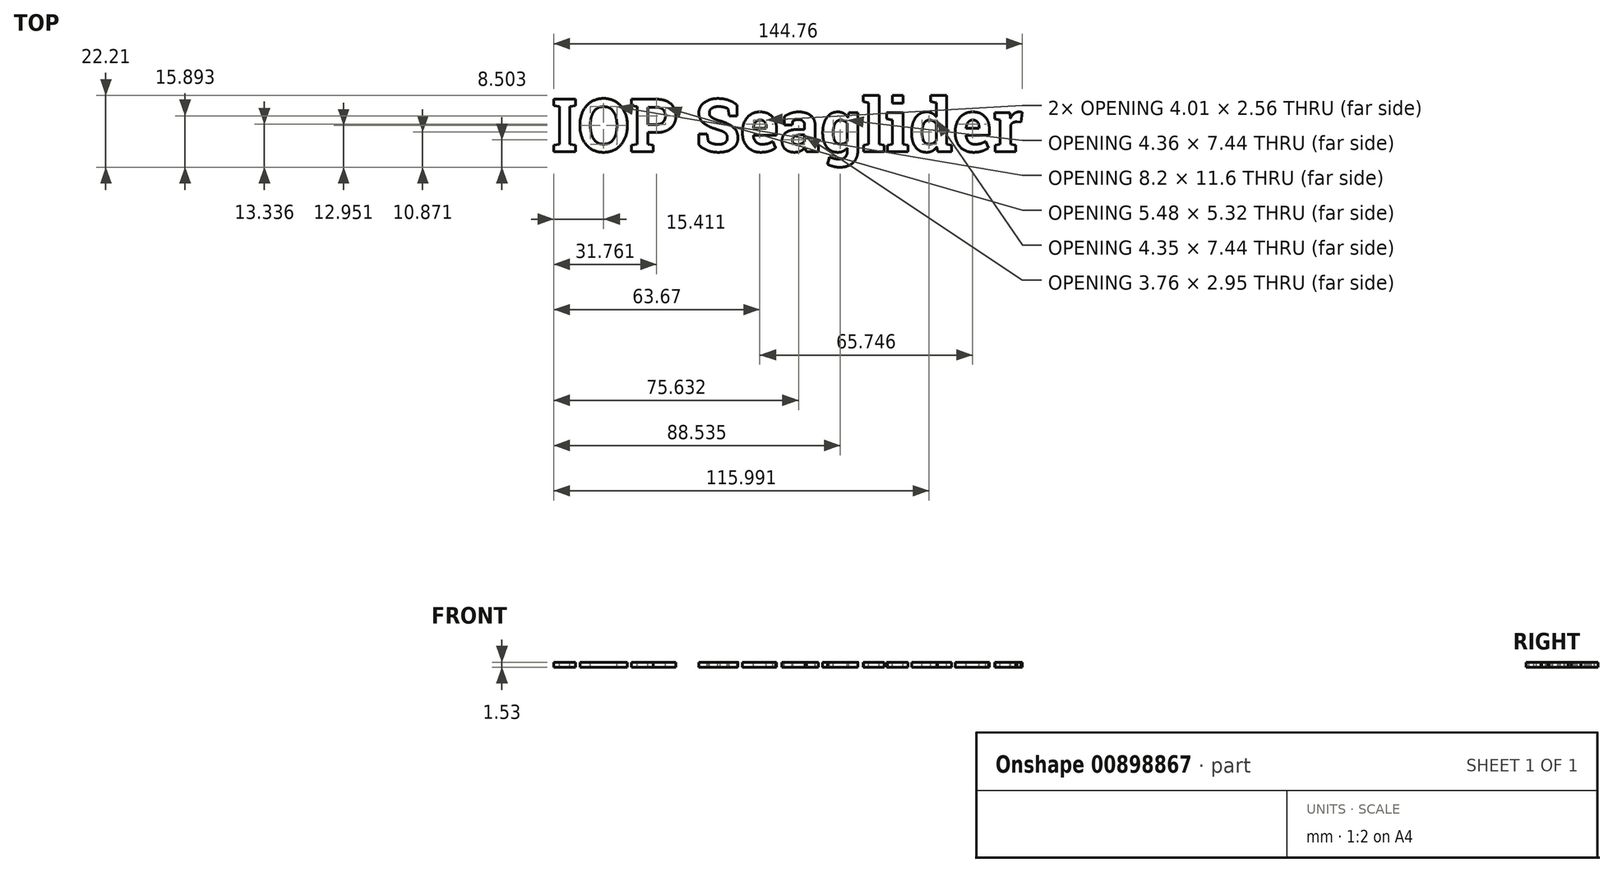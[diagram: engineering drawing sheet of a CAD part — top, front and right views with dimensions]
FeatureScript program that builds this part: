
annotation { "Feature Type Name" : "Feature", "Feature Type Description" : "" }
export const myFeature = defineFeature(function(context is Context, id is Id, definition is map)
    precondition{}
    {
        {
            var Q0;
            Q0=qCreatedBy(makeId("Top.planeOp"),FACE);
            var sketch = newSketch(context, id + "F0", { "sketchPlane" : qUnion([Q0])});
            skLineSegment(sketch, "E0.bottom", {"start": v(-73.35, 20.14) * mm, "end": v(104.45, 20.14) * mm});
            skLineSegment(sketch, "E0.top", {"start": v(-73.35, -5.26) * mm, "end": v(104.45, -5.26) * mm});
            skLineSegment(sketch, "E0.left", {"start": v(-73.35, 20.14) * mm, "end": v(-73.35, -5.26) * mm});
            skLineSegment(sketch, "E0.right", {"start": v(104.45, 20.14) * mm, "end": v(104.45, -5.26) * mm});
            skSolve(sketch);
        }
        {
            var Q0;
            Q0=makeQuery(id+"F0.imprint","IMPRINT",FACE,{"disambiguationData":[TD([[makeQuery(id+"F0.imprint","IMPRINT",EDGE,{"derivedFrom":sQuery(id+"F0.wireOp",EDGE,"E0.bottom")}),-1.0]])]});
            extrude(context, id + "F1", {"entities" : qUnion([Q0]), "depth" : 3.17 * mm, "offsetDistance" : 25.4 * mm});
        }
        {
            var Q0;
            Q0=makeQuery(id+"F1.opExtrude","CAP_FACE",FACE,{"disambiguationData":[OSD([sQuery(id+"F0.wireOp",EDGE,"E0.bottom"),sQuery(id+"F0.wireOp",EDGE,"E0.top"),sQuery(id+"F0.wireOp",EDGE,"E0.left"),sQuery(id+"F0.wireOp",EDGE,"E0.right")])],"isStart":false});
            var sketch = newSketch(context, id + "F2", { "sketchPlane" : qUnion([Q0])});
            skText(sketch, "E1", { "text": "IOP Seaglider", "fontName": "RobotoSlab-Bold.ttf"});
            const initialGuessF2  = {"E1": [-0.0586, 0, 1, 0, 0.0164]};
            skSetInitialGuess(sketch, initialGuessF2);
            skSolve(sketch);
        }
        {
            var Q0;
            Q0 = qSketchRegion(id + "F2", true);
            extrude(context, id + "F3", {"entities" : qUnion([Q0]), "operationType" : NewBodyOperationType.INTERSECT, "oppositeDirection" : true, "depth" : 1.52 * mm, "offsetDistance" : 25.4 * mm});
        }
    });
